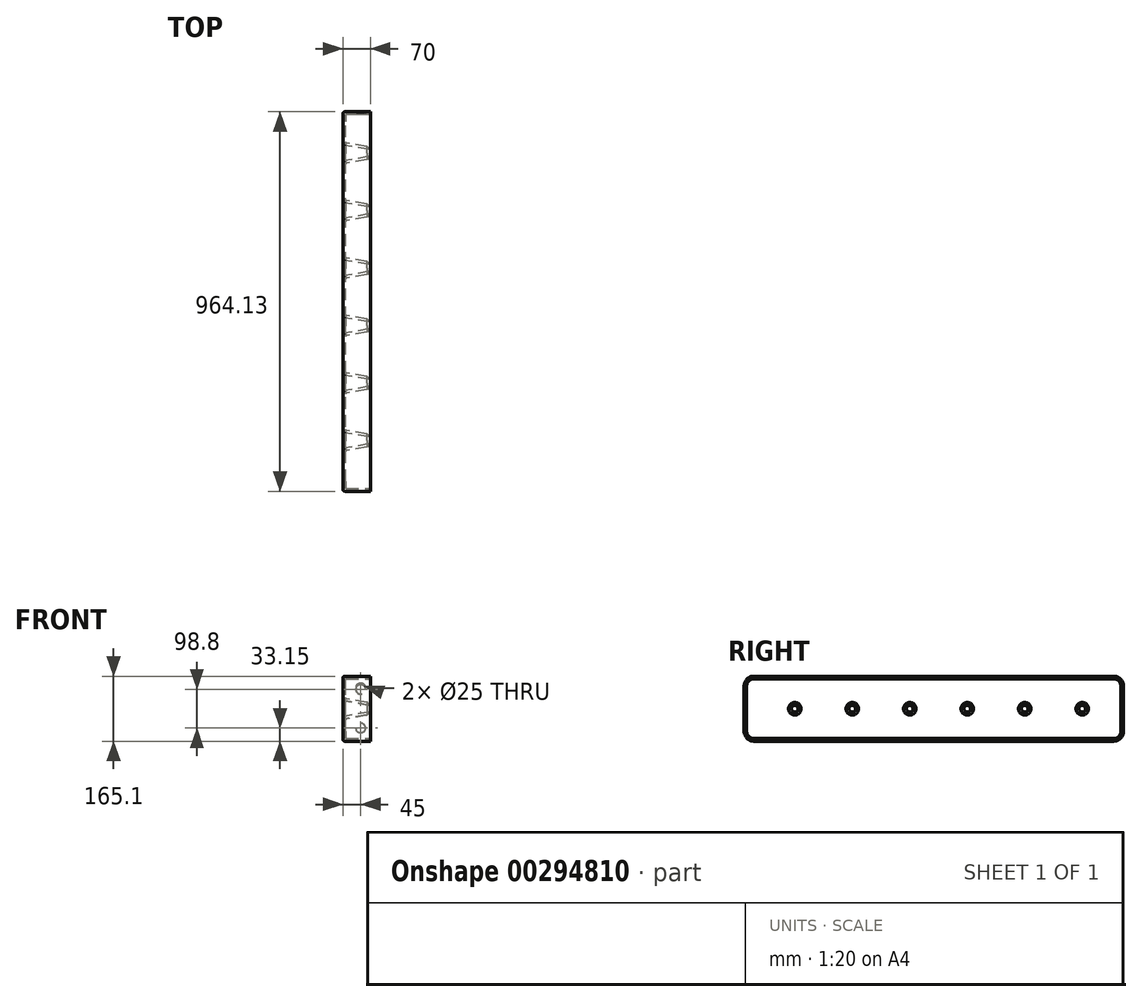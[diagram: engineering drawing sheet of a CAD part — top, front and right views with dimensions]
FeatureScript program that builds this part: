
annotation { "Feature Type Name" : "Feature", "Feature Type Description" : "" }
export const myFeature = defineFeature(function(context is Context, id is Id, definition is map)
    precondition{}
    {
        {
            var Q0;
            Q0=qCreatedBy(makeId("Right.planeOp"),FACE);
            var sketch = newSketch(context, id + "F0", { "sketchPlane" : qUnion([Q0])});
            skLineSegment(sketch, "E0.rect.bottom", {"start": v(-457.5, 82.55) * mm, "end": v(457.5, 82.55) * mm});
            skLineSegment(sketch, "E0.rect.top", {"start": v(-457.5, -82.55) * mm, "end": v(457.5, -82.55) * mm});
            skLineSegment(sketch, "E0.rect.left", {"start": v(-457.5, 82.55) * mm, "end": v(-457.5, -82.55) * mm});
            skLineSegment(sketch, "E0.rect.right", {"start": v(457.5, 82.55) * mm, "end": v(457.5, -82.55) * mm});
            skPoint(sketch, "E0.rect.middle", {"position": v(0, 0) * mm});
            skLineSegment(sketch, "E1.0", {"start": v(-447.34, 72.39) * mm, "end": v(447.34, 72.39) * mm, "construction": true});
            skLineSegment(sketch, "E1.1", {"start": v(-447.34, 72.39) * mm, "end": v(-447.34, -72.39) * mm, "construction": true});
            skLineSegment(sketch, "E1.2", {"start": v(-447.34, -72.39) * mm, "end": v(447.34, -72.39) * mm, "construction": true});
            skLineSegment(sketch, "E1.3", {"start": v(447.34, 72.39) * mm, "end": v(447.34, -72.39) * mm, "construction": true});
            skLineSegment(sketch, "E2", {"start": v(-457.5, 82.55) * mm, "end": v(457.5, -82.55) * mm, "construction": true});
            skLineSegment(sketch, "E3", {"start": v(457.5, 82.55) * mm, "end": v(-457.5, -82.55) * mm, "construction": true});
            skSolve(sketch);
        }
        {
            var Q0;
            Q0=makeQuery(id+"F0.imprint","IMPRINT",FACE,{"disambiguationData":[TD([[makeQuery(id+"F0.imprint","IMPRINT",EDGE,{"derivedFrom":sQuery(id+"F0.wireOp",EDGE,"E0.rect.bottom")}),-1.0]])]});
            extrude(context, id + "F1", {"entities" : qUnion([Q0]), "depth" : 70 * mm});
        }
        {
            var Q0;
            Q0=makeQuery(id+"F1.opExtrude","SWEPT_FACE",FACE,{"disambiguationData":[OSD([sQuery(id+"F0.wireOp",EDGE,"E0.rect.left")])]});
            extrude(context, id + "F2", {"entities" : qUnion([Q0]), "operationType" : NewBodyOperationType.ADD, "depth" : 36.63 * mm});
        }
        {
            var Q0;
            Q0=makeQuery(id+"F1.opExtrude","SWEPT_FACE",FACE,{"disambiguationData":[OSD([sQuery(id+"F0.wireOp",EDGE,"E0.rect.right")])]});
            extrude(context, id + "F3", {"entities" : qUnion([Q0]), "operationType" : NewBodyOperationType.ADD, "depth" : 12.5 * mm});
        }
        {
            var Q0;
            Q0=makeQuery(id+"F0.imprint","IMPRINT",FACE,{"disambiguationData":[TD([[makeQuery(id+"F0.imprint","IMPRINT",EDGE,{"derivedFrom":sQuery(id+"F0.wireOp",EDGE,"E0.rect.bottom")}),-1.0]])]});
            var sketch = newSketch(context, id + "F4", { "sketchPlane" : qUnion([Q0])});
            skLineSegment(sketch, "E4", {"start": v(-457.5, 0) * mm, "end": v(457.5, 0) * mm, "construction": true});
            skCircle(sketch, "E5", {"center": v(-365.13, 0) * mm, "radius": 20.32 * mm});
            skCircle(sketch, "E6", {"center": v(-73.03, 0) * mm, "radius": 20.32 * mm});
            skCircle(sketch, "E7.MirrorC", {"center": v(73.03, 0) * mm, "radius": 20.32 * mm});
            skCircle(sketch, "E8", {"center": v(-219.08, 0) * mm, "radius": 20.32 * mm});
            skCircle(sketch, "E9", {"center": v(219.08, 0) * mm, "radius": 20.32 * mm});
            skCircle(sketch, "E10", {"center": v(365.13, 0) * mm, "radius": 20.32 * mm});
            skSolve(sketch);
        }
        {
            var Q0;
            Q0=qSketchRegion(id+"F4",true);
            extrude(context, id + "F5", {"entities" : qUnion([Q0]), "operationType" : NewBodyOperationType.REMOVE, "endBound" : BoundingType.THROUGH_ALL, "depth" : 25 * mm, "hasDraft" : true, "draftAngle" : 10 * degree, "draftPullDirection" : true});
        }
        {
            var Q0;
            {var subQ0=makeQuery(id+"FMJtkyeOeprAO9Q_1.hole-4.opRevolve","SWEPT_FACE",FACE,{"disambiguationData":[OSD([sQuery(id+"FMJtkyeOeprAO9Q_1.hole-4.sketch.wireOp",EDGE,"cbore_start_line_2")])]});var subQ1=makeQuery(id+"FMJtkyeOeprAO9Q_1.hole-2.boolean.opBoolean","COPY",FACE,{"derivedFrom":makeQuery(id+"FMJtkyeOeprAO9Q_1.hole-2.opRevolve","SWEPT_FACE",FACE,{"disambiguationData":[OSD([sQuery(id+"FMJtkyeOeprAO9Q_1.hole-2.sketch.wireOp",EDGE,"cbore_start_line_2")])]})});var subQ2=sQuery(id+"F0.wireOp",EDGE,"E0.rect.top");var subQ3=makeQuery(id+"F1.opExtrude","SWEPT_FACE",FACE,{"disambiguationData":[OSD([subQ2])]});var subQ4=makeQuery(id+"FMJtkyeOeprAO9Q_1.hole-3.opRevolve","SWEPT_FACE",FACE,{"disambiguationData":[OSD([sQuery(id+"FMJtkyeOeprAO9Q_1.hole-3.sketch.wireOp",EDGE,"cbore_start_line_2")])]});var subQ5=makeQuery(id+"FMJtkyeOeprAO9Q_1.hole-3.boolean.opBoolean","COPY",FACE,{"disambiguationData":[OD(1.0)],"derivedFrom":subQ4});var subQ6=makeQuery(id+"FMJtkyeOeprAO9Q_1.hole-0.opRevolve","SWEPT_FACE",FACE,{"disambiguationData":[OSD([sQuery(id+"FMJtkyeOeprAO9Q_1.hole-0.sketch.wireOp",EDGE,"cbore_start_line_2")])]});var subQ7=makeQuery(id+"FMJtkyeOeprAO9Q_1.hole-0.boolean.opBoolean","COPY",FACE,{"disambiguationData":[OD(1.0)],"derivedFrom":subQ6});var subQ8=makeQuery(id+"FMJtkyeOeprAO9Q_1.hole-1.boolean.opBoolean","COPY",FACE,{"derivedFrom":makeQuery(id+"FMJtkyeOeprAO9Q_1.hole-1.opRevolve","SWEPT_FACE",FACE,{"disambiguationData":[OSD([sQuery(id+"FMJtkyeOeprAO9Q_1.hole-1.sketch.wireOp",EDGE,"cbore_start_line_2")])]})});var subQ9=sQuery(id+"F0.wireOp",EDGE,"E0.rect.bottom");var subQ10=makeQuery(id+"F1.opExtrude","SWEPT_FACE",FACE,{"disambiguationData":[OSD([subQ9])]});var subQ11=sQuery(id+"F0.wireOp",EDGE,"E0.rect.left");var subQ12=makeQuery(id+"F1.opExtrude","SWEPT_FACE",FACE,{"disambiguationData":[OSD([subQ11])]});var subQ13=sQuery(id+"F0.wireOp",EDGE,"E0.rect.right");var subQ14=makeQuery(id+"F1.opExtrude","SWEPT_FACE",FACE,{"disambiguationData":[OSD([subQ13])]});Q0=makeQuery(id+"FMJtkyeOeprAO9Q_1.hole-7.boolean.opBoolean","SPLIT",FACE,{"disambiguationData":[TD([subQ10,subQ3,subQ12,subQ14,subQ7,subQ8,subQ1,subQ5,makeQuery(id+"FMJtkyeOeprAO9Q_1.hole-4.boolean.opBoolean","COPY",FACE,{"disambiguationData":[OD(1.0)],"derivedFrom":subQ0}),makeQuery(id+"FMJtkyeOeprAO9Q_1.hole-5.boolean.opBoolean","COPY",FACE,{"derivedFrom":makeQuery(id+"FMJtkyeOeprAO9Q_1.hole-5.opRevolve","SWEPT_FACE",FACE,{"disambiguationData":[OSD([sQuery(id+"FMJtkyeOeprAO9Q_1.hole-5.sketch.wireOp",EDGE,"cbore_start_line_2")])]})}),makeQuery(id+"FMJtkyeOeprAO9Q_1.hole-6.boolean.opBoolean","COPY",FACE,{"derivedFrom":makeQuery(id+"FMJtkyeOeprAO9Q_1.hole-6.opRevolve","SWEPT_FACE",FACE,{"disambiguationData":[OSD([sQuery(id+"FMJtkyeOeprAO9Q_1.hole-6.sketch.wireOp",EDGE,"cbore_start_line_2")])]})}),makeQuery(id+"FMJtkyeOeprAO9Q_1.hole-7.opRevolve","SWEPT_FACE",FACE,{"disambiguationData":[OSD([sQuery(id+"FMJtkyeOeprAO9Q_1.hole-7.sketch.wireOp",EDGE,"cbore_start_line_2")])]})])],"derivedFrom":makeQuery(id+"FMJtkyeOeprAO9Q_1.hole-4.boolean.opBoolean","SPLIT",FACE,{"disambiguationData":[TD([subQ10,subQ3,subQ12,subQ14,subQ7,subQ8,subQ1,subQ5,subQ0])],"derivedFrom":makeQuery(id+"FMJtkyeOeprAO9Q_1.hole-3.boolean.opBoolean","SPLIT",FACE,{"disambiguationData":[TD([subQ10,subQ3,subQ12,subQ14,subQ7,subQ8,subQ1,subQ4])],"derivedFrom":makeQuery(id+"FMJtkyeOeprAO9Q_1.hole-0.boolean.opBoolean","SPLIT",FACE,{"disambiguationData":[TD([subQ10,subQ3,subQ12,subQ14,subQ6])],"derivedFrom":makeQuery(id+"F1.opExtrude","CAP_FACE",FACE,{"disambiguationData":[OSD([subQ9,subQ2,subQ11,subQ13])],"isStart":true})})})})});}
            fillet(context, id + "F6", {"entities" : qUnion([Q0]), "radius" : 5 * mm, "tangentPropagation" : true, "allowEdgeOverflow" : false});
        }
        {
            var Q0;
            Q0=makeQuery(id+"F2.opExtrude","CAP_EDGE",EDGE,{"disambiguationData":[OSD([sQuery(id+"F0.wireOp",EDGE,"E0.rect.bottom"),sQuery(id+"F0.wireOp",EDGE,"E0.rect.left")])],"isStart":false});
            var Q1;
            Q1=makeQuery(id+"F2.opExtrude","CAP_EDGE",EDGE,{"disambiguationData":[OSD([sQuery(id+"F0.wireOp",EDGE,"E0.rect.top"),sQuery(id+"F0.wireOp",EDGE,"E0.rect.left")])],"isStart":false});
            var Q2;
            Q2=makeQuery(id+"F3.opExtrude","CAP_EDGE",EDGE,{"disambiguationData":[OSD([sQuery(id+"F0.wireOp",EDGE,"E0.rect.top"),sQuery(id+"F0.wireOp",EDGE,"E0.rect.right")])],"isStart":false});
            var Q3;
            Q3=makeQuery(id+"F3.opExtrude","CAP_EDGE",EDGE,{"disambiguationData":[OSD([sQuery(id+"F0.wireOp",EDGE,"E0.rect.bottom"),sQuery(id+"F0.wireOp",EDGE,"E0.rect.right")])],"isStart":false});
            fillet(context, id + "F7", {"entities" : qUnion([Q0, Q1, Q2, Q3]), "radius" : 25.4 * mm, "tangentPropagation" : true, "allowEdgeOverflow" : false});
        }
        {
            var Q0;
            Q0=makeQuery(id+"F1.opExtrude","CAP_FACE",FACE,{"disambiguationData":[OSD([sQuery(id+"F0.wireOp",EDGE,"E0.rect.bottom"),sQuery(id+"F0.wireOp",EDGE,"E0.rect.top"),sQuery(id+"F0.wireOp",EDGE,"E0.rect.left"),sQuery(id+"F0.wireOp",EDGE,"E0.rect.right")])],"isStart":false});
            shell(context, id + "F8", {"entities" : qUnion([Q0]), "thickness" : 6.5 * mm});
        }
        {
            var Q0;
            {var subQ0=makeQuery(id+"FMJtkyeOeprAO9Q_1.hole-4.opRevolve","SWEPT_FACE",FACE,{"disambiguationData":[OSD([sQuery(id+"FMJtkyeOeprAO9Q_1.hole-4.sketch.wireOp",EDGE,"cbore_start_line_2")])]});var subQ1=makeQuery(id+"FMJtkyeOeprAO9Q_1.hole-2.boolean.opBoolean","COPY",FACE,{"derivedFrom":makeQuery(id+"FMJtkyeOeprAO9Q_1.hole-2.opRevolve","SWEPT_FACE",FACE,{"disambiguationData":[OSD([sQuery(id+"FMJtkyeOeprAO9Q_1.hole-2.sketch.wireOp",EDGE,"cbore_start_line_2")])]})});var subQ2=sQuery(id+"F0.wireOp",EDGE,"E0.rect.top");var subQ3=makeQuery(id+"F1.opExtrude","SWEPT_FACE",FACE,{"disambiguationData":[OSD([subQ2])]});var subQ4=makeQuery(id+"FMJtkyeOeprAO9Q_1.hole-3.opRevolve","SWEPT_FACE",FACE,{"disambiguationData":[OSD([sQuery(id+"FMJtkyeOeprAO9Q_1.hole-3.sketch.wireOp",EDGE,"cbore_start_line_2")])]});var subQ5=makeQuery(id+"FMJtkyeOeprAO9Q_1.hole-3.boolean.opBoolean","COPY",FACE,{"disambiguationData":[OD(1.0)],"derivedFrom":subQ4});var subQ6=makeQuery(id+"FMJtkyeOeprAO9Q_1.hole-0.opRevolve","SWEPT_FACE",FACE,{"disambiguationData":[OSD([sQuery(id+"FMJtkyeOeprAO9Q_1.hole-0.sketch.wireOp",EDGE,"cbore_start_line_2")])]});var subQ7=makeQuery(id+"FMJtkyeOeprAO9Q_1.hole-0.boolean.opBoolean","COPY",FACE,{"disambiguationData":[OD(1.0)],"derivedFrom":subQ6});var subQ8=makeQuery(id+"FMJtkyeOeprAO9Q_1.hole-1.boolean.opBoolean","COPY",FACE,{"derivedFrom":makeQuery(id+"FMJtkyeOeprAO9Q_1.hole-1.opRevolve","SWEPT_FACE",FACE,{"disambiguationData":[OSD([sQuery(id+"FMJtkyeOeprAO9Q_1.hole-1.sketch.wireOp",EDGE,"cbore_start_line_2")])]})});var subQ9=sQuery(id+"F0.wireOp",EDGE,"E0.rect.bottom");var subQ10=makeQuery(id+"F1.opExtrude","SWEPT_FACE",FACE,{"disambiguationData":[OSD([subQ9])]});var subQ11=sQuery(id+"F0.wireOp",EDGE,"E0.rect.left");var subQ12=makeQuery(id+"F1.opExtrude","SWEPT_FACE",FACE,{"disambiguationData":[OSD([subQ11])]});var subQ13=sQuery(id+"F0.wireOp",EDGE,"E0.rect.right");var subQ14=makeQuery(id+"F1.opExtrude","SWEPT_FACE",FACE,{"disambiguationData":[OSD([subQ13])]});Q0=makeQuery(id+"F8.opShell","OFFSET_FACE",FACE,{"disambiguationData":[OSD([subQ9,subQ2,subQ11,subQ13]),TDD([makeQuery(id+"FMJtkyeOeprAO9Q_1.hole-7.boolean.opBoolean","SPLIT",FACE,{"disambiguationData":[TD([subQ10,subQ3,subQ12,subQ14,subQ7,subQ8,subQ1,subQ5,makeQuery(id+"FMJtkyeOeprAO9Q_1.hole-4.boolean.opBoolean","COPY",FACE,{"disambiguationData":[OD(1.0)],"derivedFrom":subQ0}),makeQuery(id+"FMJtkyeOeprAO9Q_1.hole-5.boolean.opBoolean","COPY",FACE,{"derivedFrom":makeQuery(id+"FMJtkyeOeprAO9Q_1.hole-5.opRevolve","SWEPT_FACE",FACE,{"disambiguationData":[OSD([sQuery(id+"FMJtkyeOeprAO9Q_1.hole-5.sketch.wireOp",EDGE,"cbore_start_line_2")])]})}),makeQuery(id+"FMJtkyeOeprAO9Q_1.hole-6.boolean.opBoolean","COPY",FACE,{"derivedFrom":makeQuery(id+"FMJtkyeOeprAO9Q_1.hole-6.opRevolve","SWEPT_FACE",FACE,{"disambiguationData":[OSD([sQuery(id+"FMJtkyeOeprAO9Q_1.hole-6.sketch.wireOp",EDGE,"cbore_start_line_2")])]})}),makeQuery(id+"FMJtkyeOeprAO9Q_1.hole-7.opRevolve","SWEPT_FACE",FACE,{"disambiguationData":[OSD([sQuery(id+"FMJtkyeOeprAO9Q_1.hole-7.sketch.wireOp",EDGE,"cbore_start_line_2")])]})])],"derivedFrom":makeQuery(id+"FMJtkyeOeprAO9Q_1.hole-4.boolean.opBoolean","SPLIT",FACE,{"disambiguationData":[TD([subQ10,subQ3,subQ12,subQ14,subQ7,subQ8,subQ1,subQ5,subQ0])],"derivedFrom":makeQuery(id+"FMJtkyeOeprAO9Q_1.hole-3.boolean.opBoolean","SPLIT",FACE,{"disambiguationData":[TD([subQ10,subQ3,subQ12,subQ14,subQ7,subQ8,subQ1,subQ4])],"derivedFrom":makeQuery(id+"FMJtkyeOeprAO9Q_1.hole-0.boolean.opBoolean","SPLIT",FACE,{"disambiguationData":[TD([subQ10,subQ3,subQ12,subQ14,subQ6])],"derivedFrom":makeQuery(id+"F1.opExtrude","CAP_FACE",FACE,{"disambiguationData":[OSD([subQ9,subQ2,subQ11,subQ13])],"isStart":true})})})})})])]});}
            fillet(context, id + "F9", {"entities" : qUnion([Q0]), "radius" : 3.17 * mm, "tangentPropagation" : true, "allowEdgeOverflow" : false});
        }
        {
            var Q0;
            {var subQ0=sQuery(id+"F4.wireOp",EDGE,"E5");var subQ1=sQuery(id+"F0.wireOp",EDGE,"E0.rect.right");var subQ2=sQuery(id+"F0.wireOp",EDGE,"E0.rect.left");var subQ3=sQuery(id+"F0.wireOp",EDGE,"E0.rect.top");var subQ4=sQuery(id+"F0.wireOp",EDGE,"E0.rect.bottom");Q0=makeQuery(id+"F8.opShell","OFFSET_EDGE",EDGE,{"disambiguationData":[OSD([subQ4,subQ3,subQ2,subQ1,subQ0]),TDD([makeQuery(id+"F5.boolean.opBoolean","INTERSECT",EDGE,{"derivedFrom":[makeQuery(id+"F3.boolean.opBoolean","MERGE",FACE,{"derivedFrom":[makeQuery(id+"F2.boolean.opBoolean","MERGE",FACE,{"derivedFrom":[makeQuery(id+"F1.opExtrude","CAP_FACE",FACE,{"disambiguationData":[OSD([subQ4,subQ3,subQ2,subQ1])],"isStart":false}),makeQuery(id+"F2.opExtrude","SWEPT_FACE",FACE,{"disambiguationData":[OSD([subQ2]),TDD([makeQuery(id+"F1.opExtrude","CAP_EDGE",EDGE,{"disambiguationData":[OSD([subQ2])],"isStart":false})])]})]}),makeQuery(id+"F3.opExtrude","SWEPT_FACE",FACE,{"disambiguationData":[OSD([subQ1]),TDD([makeQuery(id+"F1.opExtrude","CAP_EDGE",EDGE,{"disambiguationData":[OSD([subQ1])],"isStart":false})])]})]}),makeQuery(id+"F5.opExtrude","SWEPT_FACE",FACE,{"disambiguationData":[OSD([subQ0])]})]})])]});}
            var Q1;
            {var subQ0=sQuery(id+"F4.wireOp",EDGE,"E8");var subQ1=sQuery(id+"F0.wireOp",EDGE,"E0.rect.right");var subQ2=sQuery(id+"F0.wireOp",EDGE,"E0.rect.left");var subQ3=sQuery(id+"F0.wireOp",EDGE,"E0.rect.top");var subQ4=sQuery(id+"F0.wireOp",EDGE,"E0.rect.bottom");Q1=makeQuery(id+"F8.opShell","OFFSET_EDGE",EDGE,{"disambiguationData":[OSD([subQ4,subQ3,subQ2,subQ1,subQ0]),TDD([makeQuery(id+"F5.boolean.opBoolean","INTERSECT",EDGE,{"derivedFrom":[makeQuery(id+"F3.boolean.opBoolean","MERGE",FACE,{"derivedFrom":[makeQuery(id+"F2.boolean.opBoolean","MERGE",FACE,{"derivedFrom":[makeQuery(id+"F1.opExtrude","CAP_FACE",FACE,{"disambiguationData":[OSD([subQ4,subQ3,subQ2,subQ1])],"isStart":false}),makeQuery(id+"F2.opExtrude","SWEPT_FACE",FACE,{"disambiguationData":[OSD([subQ2]),TDD([makeQuery(id+"F1.opExtrude","CAP_EDGE",EDGE,{"disambiguationData":[OSD([subQ2])],"isStart":false})])]})]}),makeQuery(id+"F3.opExtrude","SWEPT_FACE",FACE,{"disambiguationData":[OSD([subQ1]),TDD([makeQuery(id+"F1.opExtrude","CAP_EDGE",EDGE,{"disambiguationData":[OSD([subQ1])],"isStart":false})])]})]}),makeQuery(id+"F5.opExtrude","SWEPT_FACE",FACE,{"disambiguationData":[OSD([subQ0])]})]})])]});}
            var Q2;
            {var subQ0=sQuery(id+"F4.wireOp",EDGE,"E6");var subQ1=sQuery(id+"F0.wireOp",EDGE,"E0.rect.right");var subQ2=sQuery(id+"F0.wireOp",EDGE,"E0.rect.left");var subQ3=sQuery(id+"F0.wireOp",EDGE,"E0.rect.top");var subQ4=sQuery(id+"F0.wireOp",EDGE,"E0.rect.bottom");Q2=makeQuery(id+"F8.opShell","OFFSET_EDGE",EDGE,{"disambiguationData":[OSD([subQ4,subQ3,subQ2,subQ1,subQ0]),TDD([makeQuery(id+"F5.boolean.opBoolean","INTERSECT",EDGE,{"derivedFrom":[makeQuery(id+"F3.boolean.opBoolean","MERGE",FACE,{"derivedFrom":[makeQuery(id+"F2.boolean.opBoolean","MERGE",FACE,{"derivedFrom":[makeQuery(id+"F1.opExtrude","CAP_FACE",FACE,{"disambiguationData":[OSD([subQ4,subQ3,subQ2,subQ1])],"isStart":false}),makeQuery(id+"F2.opExtrude","SWEPT_FACE",FACE,{"disambiguationData":[OSD([subQ2]),TDD([makeQuery(id+"F1.opExtrude","CAP_EDGE",EDGE,{"disambiguationData":[OSD([subQ2])],"isStart":false})])]})]}),makeQuery(id+"F3.opExtrude","SWEPT_FACE",FACE,{"disambiguationData":[OSD([subQ1]),TDD([makeQuery(id+"F1.opExtrude","CAP_EDGE",EDGE,{"disambiguationData":[OSD([subQ1])],"isStart":false})])]})]}),makeQuery(id+"F5.opExtrude","SWEPT_FACE",FACE,{"disambiguationData":[OSD([subQ0])]})]})])]});}
            var Q3;
            {var subQ0=sQuery(id+"F4.wireOp",EDGE,"E7.MirrorC");var subQ1=sQuery(id+"F0.wireOp",EDGE,"E0.rect.right");var subQ2=sQuery(id+"F0.wireOp",EDGE,"E0.rect.left");var subQ3=sQuery(id+"F0.wireOp",EDGE,"E0.rect.top");var subQ4=sQuery(id+"F0.wireOp",EDGE,"E0.rect.bottom");Q3=makeQuery(id+"F8.opShell","OFFSET_EDGE",EDGE,{"disambiguationData":[OSD([subQ4,subQ3,subQ2,subQ1,subQ0]),TDD([makeQuery(id+"F5.boolean.opBoolean","INTERSECT",EDGE,{"derivedFrom":[makeQuery(id+"F3.boolean.opBoolean","MERGE",FACE,{"derivedFrom":[makeQuery(id+"F2.boolean.opBoolean","MERGE",FACE,{"derivedFrom":[makeQuery(id+"F1.opExtrude","CAP_FACE",FACE,{"disambiguationData":[OSD([subQ4,subQ3,subQ2,subQ1])],"isStart":false}),makeQuery(id+"F2.opExtrude","SWEPT_FACE",FACE,{"disambiguationData":[OSD([subQ2]),TDD([makeQuery(id+"F1.opExtrude","CAP_EDGE",EDGE,{"disambiguationData":[OSD([subQ2])],"isStart":false})])]})]}),makeQuery(id+"F3.opExtrude","SWEPT_FACE",FACE,{"disambiguationData":[OSD([subQ1]),TDD([makeQuery(id+"F1.opExtrude","CAP_EDGE",EDGE,{"disambiguationData":[OSD([subQ1])],"isStart":false})])]})]}),makeQuery(id+"F5.opExtrude","SWEPT_FACE",FACE,{"disambiguationData":[OSD([subQ0])]})]})])]});}
            var Q4;
            {var subQ0=sQuery(id+"F4.wireOp",EDGE,"E9");var subQ1=sQuery(id+"F0.wireOp",EDGE,"E0.rect.right");var subQ2=sQuery(id+"F0.wireOp",EDGE,"E0.rect.left");var subQ3=sQuery(id+"F0.wireOp",EDGE,"E0.rect.top");var subQ4=sQuery(id+"F0.wireOp",EDGE,"E0.rect.bottom");Q4=makeQuery(id+"F8.opShell","OFFSET_EDGE",EDGE,{"disambiguationData":[OSD([subQ4,subQ3,subQ2,subQ1,subQ0]),TDD([makeQuery(id+"F5.boolean.opBoolean","INTERSECT",EDGE,{"derivedFrom":[makeQuery(id+"F3.boolean.opBoolean","MERGE",FACE,{"derivedFrom":[makeQuery(id+"F2.boolean.opBoolean","MERGE",FACE,{"derivedFrom":[makeQuery(id+"F1.opExtrude","CAP_FACE",FACE,{"disambiguationData":[OSD([subQ4,subQ3,subQ2,subQ1])],"isStart":false}),makeQuery(id+"F2.opExtrude","SWEPT_FACE",FACE,{"disambiguationData":[OSD([subQ2]),TDD([makeQuery(id+"F1.opExtrude","CAP_EDGE",EDGE,{"disambiguationData":[OSD([subQ2])],"isStart":false})])]})]}),makeQuery(id+"F3.opExtrude","SWEPT_FACE",FACE,{"disambiguationData":[OSD([subQ1]),TDD([makeQuery(id+"F1.opExtrude","CAP_EDGE",EDGE,{"disambiguationData":[OSD([subQ1])],"isStart":false})])]})]}),makeQuery(id+"F5.opExtrude","SWEPT_FACE",FACE,{"disambiguationData":[OSD([subQ0])]})]})])]});}
            var Q5;
            {var subQ0=sQuery(id+"F4.wireOp",EDGE,"E10");var subQ1=sQuery(id+"F0.wireOp",EDGE,"E0.rect.right");var subQ2=sQuery(id+"F0.wireOp",EDGE,"E0.rect.left");var subQ3=sQuery(id+"F0.wireOp",EDGE,"E0.rect.top");var subQ4=sQuery(id+"F0.wireOp",EDGE,"E0.rect.bottom");Q5=makeQuery(id+"F8.opShell","OFFSET_EDGE",EDGE,{"disambiguationData":[OSD([subQ4,subQ3,subQ2,subQ1,subQ0]),TDD([makeQuery(id+"F5.boolean.opBoolean","INTERSECT",EDGE,{"derivedFrom":[makeQuery(id+"F3.boolean.opBoolean","MERGE",FACE,{"derivedFrom":[makeQuery(id+"F2.boolean.opBoolean","MERGE",FACE,{"derivedFrom":[makeQuery(id+"F1.opExtrude","CAP_FACE",FACE,{"disambiguationData":[OSD([subQ4,subQ3,subQ2,subQ1])],"isStart":false}),makeQuery(id+"F2.opExtrude","SWEPT_FACE",FACE,{"disambiguationData":[OSD([subQ2]),TDD([makeQuery(id+"F1.opExtrude","CAP_EDGE",EDGE,{"disambiguationData":[OSD([subQ2])],"isStart":false})])]})]}),makeQuery(id+"F3.opExtrude","SWEPT_FACE",FACE,{"disambiguationData":[OSD([subQ1]),TDD([makeQuery(id+"F1.opExtrude","CAP_EDGE",EDGE,{"disambiguationData":[OSD([subQ1])],"isStart":false})])]})]}),makeQuery(id+"F5.opExtrude","SWEPT_FACE",FACE,{"disambiguationData":[OSD([subQ0])]})]})])]});}
            chamfer(context, id + "F10", {"entities" : qUnion([Q0, Q1, Q2, Q3, Q4, Q5]), "width" : 10 * mm, "tangentPropagation" : true});
        }
        {
            var Q0;
            Q0=makeQuery(id+"F3.opExtrude","CAP_FACE",FACE,{"disambiguationData":[OSD([sQuery(id+"F0.wireOp",EDGE,"E0.rect.right")])],"isStart":false});
            var sketch = newSketch(context, id + "F11", { "sketchPlane" : qUnion([Q0])});
            skCircle(sketch, "E11", {"center": v(-45, 49.4) * mm, "radius": 12.5 * mm});
            skCircle(sketch, "E12", {"center": v(-45, -49.4) * mm, "radius": 12.5 * mm});
            skSolve(sketch);
        }
        {
            var Q0;
            {var subQ0=sQuery(id+"F11.wireOp",EDGE,"E11");var subQ1=sQuery(id+"F0.wireOp",EDGE,"E0.rect.right");var subQ2=makeQuery(id+"F7.opFillet","BLEND_EDGE",EDGE,{"blendedFrom":[makeQuery(id+"F3.opExtrude","CAP_EDGE",EDGE,{"disambiguationData":[OSD([sQuery(id+"F0.wireOp",EDGE,"E0.rect.bottom"),subQ1])],"isStart":false}),makeQuery(id+"F3.opExtrude","CAP_FACE",FACE,{"disambiguationData":[OSD([subQ1])],"isStart":false})],"blendedInto":[makeQuery(id+"F3.opExtrude","CAP_FACE",FACE,{"disambiguationData":[OSD([subQ1])],"isStart":false})]});var subQ3=makeQuery(id+"F11.imprint","INTERSECT",VERTEX,{"disambiguationData":[OD(0.0)],"derivedFrom":[subQ2,subQ0]});Q0=makeQuery(id+"F11.imprint","IMPRINT",FACE,{"disambiguationData":[TD([[makeQuery(id+"F11.imprint","IMPRINT",EDGE,{"disambiguationData":[TD([[subQ3,-1.0]])],"derivedFrom":subQ0}),1.0]])]});}
            var Q1;
            {var subQ0=sQuery(id+"F11.wireOp",EDGE,"E11");var subQ1=sQuery(id+"F0.wireOp",EDGE,"E0.rect.right");var subQ2=makeQuery(id+"F7.opFillet","BLEND_EDGE",EDGE,{"blendedFrom":[makeQuery(id+"F3.opExtrude","CAP_EDGE",EDGE,{"disambiguationData":[OSD([sQuery(id+"F0.wireOp",EDGE,"E0.rect.bottom"),subQ1])],"isStart":false}),makeQuery(id+"F3.opExtrude","CAP_FACE",FACE,{"disambiguationData":[OSD([subQ1])],"isStart":false})],"blendedInto":[makeQuery(id+"F3.opExtrude","CAP_FACE",FACE,{"disambiguationData":[OSD([subQ1])],"isStart":false})]});var subQ3=makeQuery(id+"F11.imprint","INTERSECT",VERTEX,{"disambiguationData":[OD(0.0)],"derivedFrom":[subQ2,subQ0]});Q1=makeQuery(id+"F11.imprint","IMPRINT",FACE,{"disambiguationData":[TD([[makeQuery(id+"F11.imprint","IMPRINT",EDGE,{"disambiguationData":[TD([[subQ3,1.0]])],"derivedFrom":subQ0}),1.0]])]});}
            var Q2;
            {var subQ0=sQuery(id+"F11.wireOp",EDGE,"E12");var subQ1=sQuery(id+"F0.wireOp",EDGE,"E0.rect.right");var subQ2=makeQuery(id+"F7.opFillet","BLEND_EDGE",EDGE,{"blendedFrom":[makeQuery(id+"F3.opExtrude","CAP_EDGE",EDGE,{"disambiguationData":[OSD([sQuery(id+"F0.wireOp",EDGE,"E0.rect.top"),subQ1])],"isStart":false}),makeQuery(id+"F3.opExtrude","CAP_FACE",FACE,{"disambiguationData":[OSD([subQ1])],"isStart":false})],"blendedInto":[makeQuery(id+"F3.opExtrude","CAP_FACE",FACE,{"disambiguationData":[OSD([subQ1])],"isStart":false})]});var subQ3=makeQuery(id+"F11.imprint","INTERSECT",VERTEX,{"disambiguationData":[OD(0.0)],"derivedFrom":[subQ2,subQ0]});Q2=makeQuery(id+"F11.imprint","IMPRINT",FACE,{"disambiguationData":[TD([[makeQuery(id+"F11.imprint","IMPRINT",EDGE,{"disambiguationData":[TD([[subQ3,1.0]])],"derivedFrom":subQ0}),1.0]])]});}
            var Q3;
            {var subQ0=sQuery(id+"F11.wireOp",EDGE,"E12");var subQ1=sQuery(id+"F0.wireOp",EDGE,"E0.rect.right");var subQ2=makeQuery(id+"F7.opFillet","BLEND_EDGE",EDGE,{"blendedFrom":[makeQuery(id+"F3.opExtrude","CAP_EDGE",EDGE,{"disambiguationData":[OSD([sQuery(id+"F0.wireOp",EDGE,"E0.rect.top"),subQ1])],"isStart":false}),makeQuery(id+"F3.opExtrude","CAP_FACE",FACE,{"disambiguationData":[OSD([subQ1])],"isStart":false})],"blendedInto":[makeQuery(id+"F3.opExtrude","CAP_FACE",FACE,{"disambiguationData":[OSD([subQ1])],"isStart":false})]});var subQ3=makeQuery(id+"F11.imprint","INTERSECT",VERTEX,{"disambiguationData":[OD(0.0)],"derivedFrom":[subQ2,subQ0]});Q3=makeQuery(id+"F11.imprint","IMPRINT",FACE,{"disambiguationData":[TD([[makeQuery(id+"F11.imprint","IMPRINT",EDGE,{"disambiguationData":[TD([[subQ3,-1.0]])],"derivedFrom":subQ0}),1.0]])]});}
            extrude(context, id + "F12", {"entities" : qUnion([Q0, Q1, Q2, Q3]), "operationType" : NewBodyOperationType.REMOVE, "oppositeDirection" : true, "depth" : 25 * mm});
        }
        {
            var Q0;
            Q0=makeQuery(id+"F12.boolean.opBoolean","INTERSECT",EDGE,{"derivedFrom":[makeQuery(id+"F7.opFillet","BLEND_FACE",FACE,{"disambiguationData":[OSD([sQuery(id+"F0.wireOp",EDGE,"E0.rect.bottom"),sQuery(id+"F0.wireOp",EDGE,"E0.rect.right")])]}),makeQuery(id+"F12.opExtrude","SWEPT_FACE",FACE,{"disambiguationData":[OSD([sQuery(id+"F11.wireOp",EDGE,"E11")])]})]});
            var Q1;
            Q1=makeQuery(id+"F12.boolean.opBoolean","COPY",EDGE,{"derivedFrom":makeQuery(id+"F12.opExtrude","CAP_EDGE",EDGE,{"disambiguationData":[OSD([sQuery(id+"F11.wireOp",EDGE,"E11")])],"isStart":true})});
            var Q2;
            Q2=makeQuery(id+"F12.boolean.opBoolean","COPY",EDGE,{"derivedFrom":makeQuery(id+"F12.opExtrude","CAP_EDGE",EDGE,{"disambiguationData":[OSD([sQuery(id+"F11.wireOp",EDGE,"E12")])],"isStart":true})});
            fillet(context, id + "F13", {"entities" : qUnion([Q0, Q1, Q2]), "radius" : 2 * mm, "tangentPropagation" : true, "allowEdgeOverflow" : false});
        }
    });
